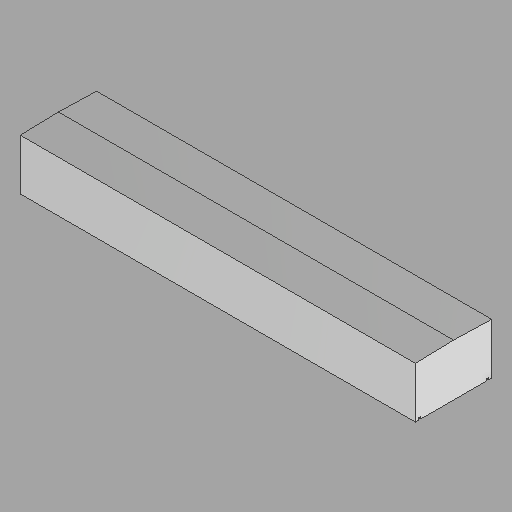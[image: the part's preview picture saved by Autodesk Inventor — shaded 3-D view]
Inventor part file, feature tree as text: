
AUTODESK INVENTOR PART (.ipt)
format: ipt  version: 2022.2 (Build 262287010, 287A)  size: 141,312 bytes
history: native  units: in
note: dims shown in document units (in); Inventor stores cm internally (conversion verified against a paired STEP export)
features: extrude x2, sketch x1, other x1
ambient origin geometry x8: Origin, YZ Plane, XZ Plane, XY Plane, X Axis, Y Axis, Z Axis, Center Point
bodies: Solid1 (feature_tree)
feature tree (4):
  sketch  "Sketch1"  dims[d0=0.125in d1=0.25in d2=0.25in d3=0.375in d4=0.25in d5=0.25in d6=0.375in d7=46.625in d8=0.0in d9=46.625in d10=0.0in]
  extrude  "Extrusion1"  Depth=0.25in
  extrude  "Extrusion2"  Depth=0.25in
  other  "Cap (3)"
